# Revit family: RN 80175 Optipress-Aquaplus-KRV-Ventil EA
name_source: partatom
category: Rohrzubehör
units: mm (PartAtom-declared; Revit-internal decimal feet)

## family parameters
Arbeitsebenenbasiert = Nein
Beim Laden mit Abzugskörper schneiden = Nein
Bemaßung runder Anschluss = Durchmesser verwenden
Gemeinsam genutzt = Nein
Immer vertikal = Ja
Teiletyp = Ventil - Zerlegung in

## types (3) — shared parameters
1.010.00.2 Blattnummer der Richtlinie = 17
1.010.00.3 Ausgabedatum (Monat) der Richtlinie = 201601
1.010.00.4 Herstellername = R. Nussbaum AG
1.010.00.5 Revisionsdatum der Datei = 20190528
1.010.00.6 Webadresse des Herstellers = http://www.nussbaum.ch
1.100.00.3 Sortiernummer für Anzeigereihenfolge = 4
1.100.00.4 Produktbezeichnung = Sicherungs- und Ringleitungsarmaturen
1.960/3L.00.8 Link (URL) = https://www.nussbaum.ch
17.700.00.4 Armaturentyp = 6
17.700.00.7 Maximale Betriebstemperatur TB [°C] = 90
17.700.00.8 Maximaler Betriebsdruck (Arbeitsdruck) ps [1.0 · 105 Pa] = 16
Connector Visibility = Nein
EnclosingSpace Visibility = Nein

## per-type parameters (varying)
| type | 1.800.00.3 TGA-Nummer | 1.810.00.3 Hersteller-Bestellnummer | 1.810.00.4 DATANORM-Nummer | 1.810.00.6 GTIN-Nummer | 17.700.00.30 Produktbeschreibung | 17.700.00.5 Nennweite DN | 17.700.00.6 kvs-Wert [m3/h] | CONNECTOR0_DIAMETER_dX_0r | CONNECTOR0_dX_00 | CONNECTOR0_dX_01 | CONNECTOR0_ref_dX | CONNECTOR1_DIAMETER_dX_0r | CONNECTOR1_dX_00 | CONNECTOR1_dX_01 | CONNECTOR1_ref_dX | R. Nussbaum AG 80175.24 de Visibility | R. Nussbaum AG 80175.25 de Visibility | R. Nussbaum AG 80175.26 de Visibility |
| DN 20 | 0040310000000000000000000000090070000000000000000100000000 | 80175.24 | 80175.24 | 7612945737342 | 80175.24, Optipress-Aquaplus-KRV-Ventil EA, DN=20 | 20 | 10.8 | 20 mm | 62 mm | 38 mm | 38 mm | 20 mm | 38 mm | 62 mm | 38 mm | Ja | Nein | Nein |
| DN 25 | 0040310000000000000000000000090070000000000000000200000000 | 80175.25 | 80175.25 | 7612945737502 | 80175.25, Optipress-Aquaplus-KRV-Ventil EA, DN=25 | 25 | 16.8 | 25 mm  [stored 0.082021 ft] | 68 mm | 44 mm | 44 mm | 25 mm  [stored 0.082021 ft] | 45 mm | 69 mm | 45 mm | Nein | Ja | Nein |
| DN 32 | 0040310000000000000000000000090070000000000000000300000000 | 80175.26 | 80175.26 | 7612945735331 | 80175.26, Optipress-Aquaplus-KRV-Ventil EA, DN=32 | 32 | 31.2 | 25 mm  [stored 0.082021 ft] | 80 mm | 54 mm | 54 mm | 25 mm  [stored 0.082021 ft] | 54 mm | 80 mm | 54 mm | Nein | Nein | Ja |

note: [stored X ft] marks values corroborated as IEEE doubles in the binary element streams (Revit-internal decimal feet)

## geometry (parser evidence)
native form markers: Sweep x2
no freeform markers — native parametric forms only
